# Revit family: 2M_Butterfly Valve_UNIVAL_BLN-0305 - 50-300 mm
name_source: partatom
category: Pipe Accessories
revit_build: Autodesk Revit 2016 (Build: 20150220_1215(x64)
units: mm (PartAtom-declared; Revit-internal decimal feet)

## family parameters
Always vertical = Yes
Cut with Voids When Loaded = No
OmniClass Number = 23.65.55.14.17
OmniClass Title = Adjusting/Controlling Valves for Liquid Services
Part Type = Valve - Breaks Into
Round Connector Dimension = Use Diameter
Shared = No
Work Plane-Based = No

## types (9) — shared parameters
Body Material = Ductile iron
Certifications = TSE EAC CE
Connection Type = Lug
Description = Lug type butterfly valve
Description TR = Lug tipi kelebek vana
Disc Material = Stainless steel
Gasket Material = EPDM
K Coefficient Table = Butterfly Valve Full Open
Loss Method = K Coefficient from Table
Manufacturer = Giacomini Unival
Giacomini Unival
Max. Working Pressure = 16.5 Bar
Max. Working Temperature = EPDM 120°C (water)
Pressure Rating = PN25
Seat Material = EPDM
Standard No = TS EN 593+A1
T = -10 mm  [stored -0.0328084 ft]
URL = http://www.unival.com.tr

## per-type parameters (varying)
| type | A | B | Body_r | D | DN | Disc_r | E | Kv | LugHole_pcs | Lug_angle | Lug_do | LugrAxis_dist | Max Diff. Pressure (Allowed) | Model | Operator Type | Stem_D | Stem_top_h | d |
| DN100 | 180 mm | 100 mm  [stored 0.328084 ft] | 73 mm  [stored 0.239501 ft] | 90 mm  [stored 0.295276 ft] | 100 mm | 50 mm  [stored 0.164042 ft] | 52 mm | 760 | 8 | 22.50° | 30 mm  [stored 0.0984252 ft] | 85 mm  [stored 0.278871 ft] | 3 Bar | BLN-0305X100 | M_Handle - Curved : Lever_260mm | 35 mm  [stored 0.114829 ft] | 1 mm  [stored 0.00328084 ft] | 16 mm  [stored 0.0524934 ft] |
| DN250 | 274 mm | 200 mm | 148 mm | 125 mm | 250 mm | 125 mm | 69 mm | 5050 | 12 | 30.00° | 38 mm  [stored 0.124672 ft] | 160 mm | 1.5 Bar | BLN-0305X250 | M_Handle - Curved : Lever_416mm | 46 mm  [stored 0.150919 ft] | 26 mm | 24 mm  [stored 0.0787402 ft] |
| DN50 | 140 mm | 69 mm | 48 mm  [stored 0.15748 ft] | 90 mm  [stored 0.295276 ft] | 50 mm | 25 mm  [stored 0.082021 ft] | 43 mm  [stored 0.141076 ft] | 115 | 4 | 90.00° | 30 mm  [stored 0.0984252 ft] | 60 mm  [stored 0.19685 ft] | 3 Bar | BLN-0305X050 | M_Handle - Curved : Lever_260mm | 29 mm | 1 mm  [stored 0.00328084 ft] | 16 mm  [stored 0.0524934 ft] |
| DN65 | 152 mm | 76 mm  [stored 0.249344 ft] | 56 mm  [stored 0.183727 ft] | 90 mm  [stored 0.295276 ft] | 65 mm | 33 mm | 45 mm  [stored 0.147638 ft] | 255 | 4 | 90.00° | 30 mm  [stored 0.0984252 ft] | 68 mm | 3 Bar | BLN-0305X065 | M_Handle - Curved : Lever_260mm | 30 mm  [stored 0.0984252 ft] | 1 mm  [stored 0.00328084 ft] | 16 mm  [stored 0.0524934 ft] |
| DN80 | 160 mm | 85 mm  [stored 0.278871 ft] | 63 mm  [stored 0.206693 ft] | 90 mm  [stored 0.295276 ft] | 80 mm | 40 mm  [stored 0.131234 ft] | 46 mm  [stored 0.150919 ft] | 375 | 4 | 90.00° | 30 mm  [stored 0.0984252 ft] | 75 mm | 3 Bar | BLN-0305X080 | M_Handle - Curved : Lever_260mm | 31 mm | 1 mm  [stored 0.00328084 ft] | 16 mm  [stored 0.0524934 ft] |
| DN125 | 191 mm | 120 mm | 86 mm | 90 mm  [stored 0.295276 ft] | 125 mm | 63 mm  [stored 0.206693 ft] | 56 mm  [stored 0.183727 ft] | 1030 | 8 | 22.50° | 30 mm  [stored 0.0984252 ft] | 98 mm  [stored 0.321522 ft] | 3 Bar | BLN-0305X125 | M_Handle - Curved : Lever_260mm | 38 mm  [stored 0.124672 ft] | 1 mm  [stored 0.00328084 ft] | 16 mm  [stored 0.0524934 ft] |
| DN150 | 202 mm | 132 mm | 98 mm  [stored 0.321522 ft] | 90 mm  [stored 0.295276 ft] | 150 mm | 75 mm | 57 mm | 1790 | 8 | 22.50° | 30 mm  [stored 0.0984252 ft] | 110 mm | 3 Bar | BLN-0305X150 | M_Handle - Curved : Lever_260mm | 38 mm  [stored 0.124672 ft] | 1 mm  [stored 0.00328084 ft] | 16 mm  [stored 0.0524934 ft] |
| DN200 | 237 mm | 160 mm | 123 mm | 125 mm | 200 mm | 100 mm  [stored 0.328084 ft] | 60 mm  [stored 0.19685 ft] | 3450 | 12 | 30.00° | 34 mm | 135 mm | 3 Bar | BLN-0305X200 | M_Handle - Curved : Lever_326mm | 40 mm  [stored 0.131234 ft] | 23 mm  [stored 0.0754593 ft] | 20 mm  [stored 0.0656168 ft] |
| DN300 | 312 mm | 230 mm | 173 mm | 125 mm | 300 mm | 150 mm | 80 mm  [stored 0.262467 ft] | 7420 | 12 | 30.00° | 38 mm  [stored 0.124672 ft] | 185 mm | 1.5 Bar | BLN-0305X300 | M_Handle - Curved : Lever_416mm | 53 mm | 26 mm | 24 mm  [stored 0.0787402 ft] |

note: [stored X ft] marks values corroborated as IEEE doubles in the binary element streams (Revit-internal decimal feet)

## geometry (parser evidence)
native form markers: Sweep x8
no freeform markers — native parametric forms only
